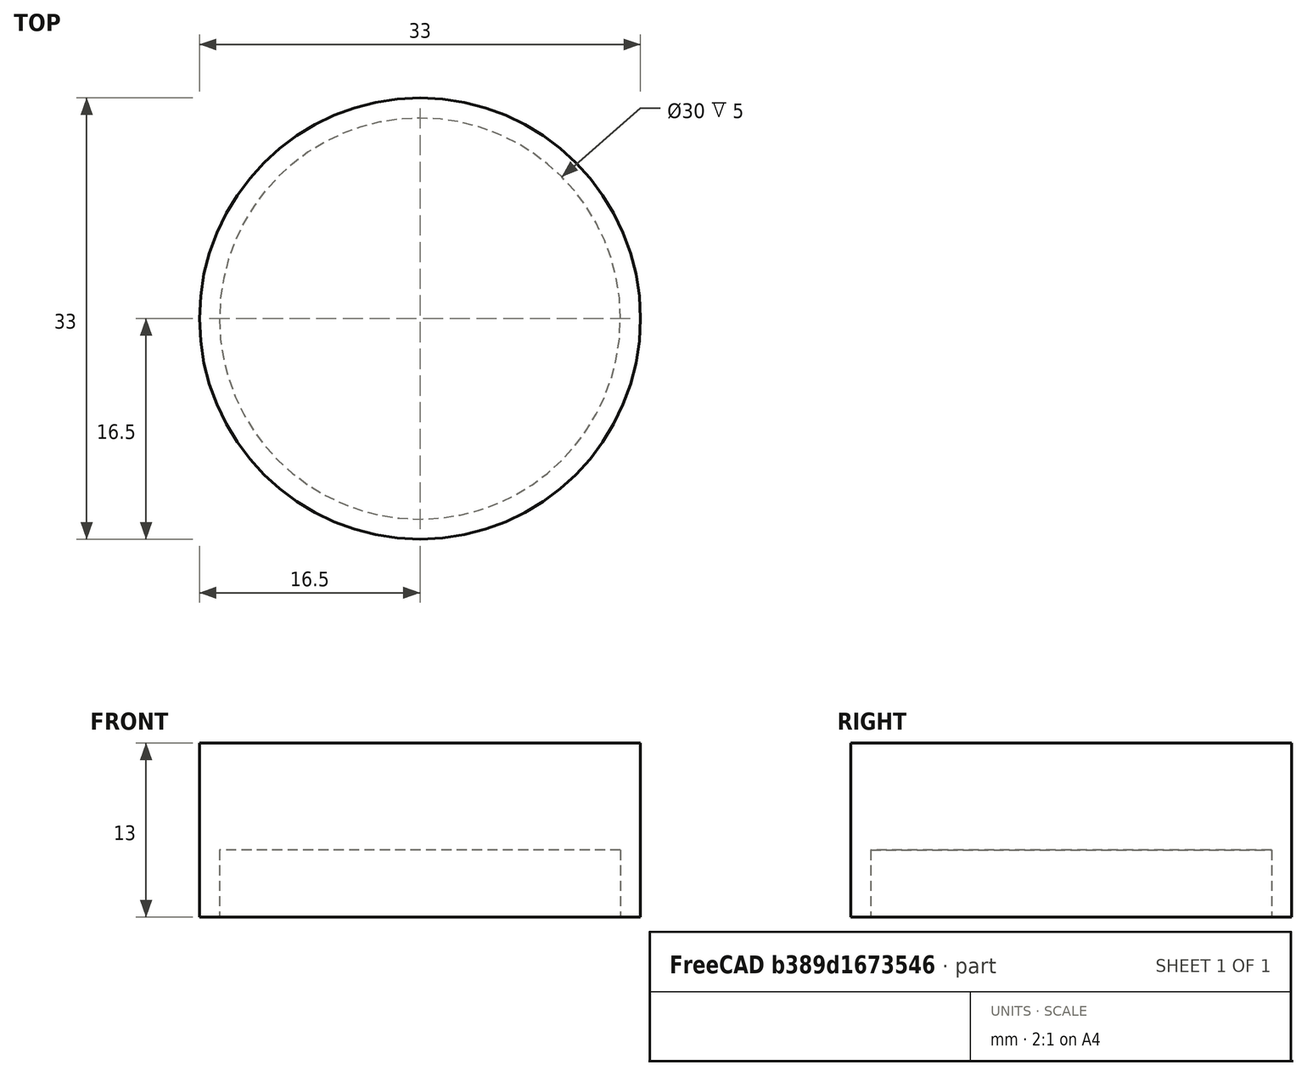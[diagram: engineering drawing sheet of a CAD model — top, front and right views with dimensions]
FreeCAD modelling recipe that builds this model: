
FCSTD DOCUMENT  (FreeCAD 1.1R20260414 (Git shallow))
Label: Удлинитель
License: All rights reserved
LicenseURL: https://en.wikipedia.org/wiki/All_rights_reserved
objects: App::Point×1, Sketcher::SketchObject×1, PartDesign::Revolution×1, PartDesign::Body×1
note: 6 computed .brp shape members not serialized (recipe doc carries the construction recipe); baked Part::Feature solids carry a one-line shape summary decoded from their .brp

FEATURE [App::Point] Origin001  label="Начало координат"
  Role = Origin
FEATURE [Sketcher::SketchObject] Sketch
  ArcFitTolerance = 1e-06
  AttachmentSupport = -> [Origin]
  ExternalTypes = [0]
  FullyConstrained = true
  MakeInternals = false
  MapMode = 5
  Placement = pos=(0,0,0) rot=(1,0,0;1.5708rad)
  _ExternalGeoVersion = 1
  sketch-geometry (6):
    g0: LineSegment StartX=0 StartY=13 StartZ=0 EndX=0 EndY=5 EndZ=0
    g1: LineSegment StartX=0 StartY=5 StartZ=0 EndX=15 EndY=5 EndZ=0
    g2: LineSegment StartX=15 StartY=5 StartZ=0 EndX=15 EndY=0 EndZ=0
    g3: LineSegment StartX=15 StartY=0 StartZ=0 EndX=16.5 EndY=0 EndZ=0
    g4: LineSegment StartX=16.5 StartY=0 StartZ=0 EndX=16.5 EndY=13 EndZ=0
    g5: LineSegment StartX=16.5 StartY=13 StartZ=0 EndX=0 EndY=13 EndZ=0
  constraints (18):
    c: Coincident(g0,g1)
    c: Coincident(g1,g2)
    c: Vertical(g2)
    c: Coincident(g2,g3)
    c: Coincident(g3,g4)
    c: Coincident(g4,g5)
    c: Coincident(g5,g0)
    c: Horizontal(g5)
    c: Horizontal(g3)
    c: Horizontal(g1)
    c: Vertical(g0)
    c: Vertical(g4)
    c: PointOnObject(g2,g-1)
    c: PointOnObject(g0,g-2)
    c: DistanceX(g-1,g2) = 15
    c: DistanceY(g2,g2) = 5
    c: DistanceY(g0,g0) = 8
    c: DistanceX(g3,g3) = 1.5
FEATURE [PartDesign::Revolution] Revolution
  Angle = 360
  Angle2 = 0
  Axis = (0,2e-16,1)
  Base = (0,0,0)
  FuseOrder = 0
  Profile = -> Sketch
  ReferenceAxis = -> Sketch [V_Axis]
  Refine = true
  Reversed = true
  Suppressed = false
  Type = 0
FEATURE [PartDesign::Body] Body  label="Тело"
  AllowCompound = true
  Group = -> [Sketch,Revolution]
  Origin = -> Origin
  Tip = -> Revolution
